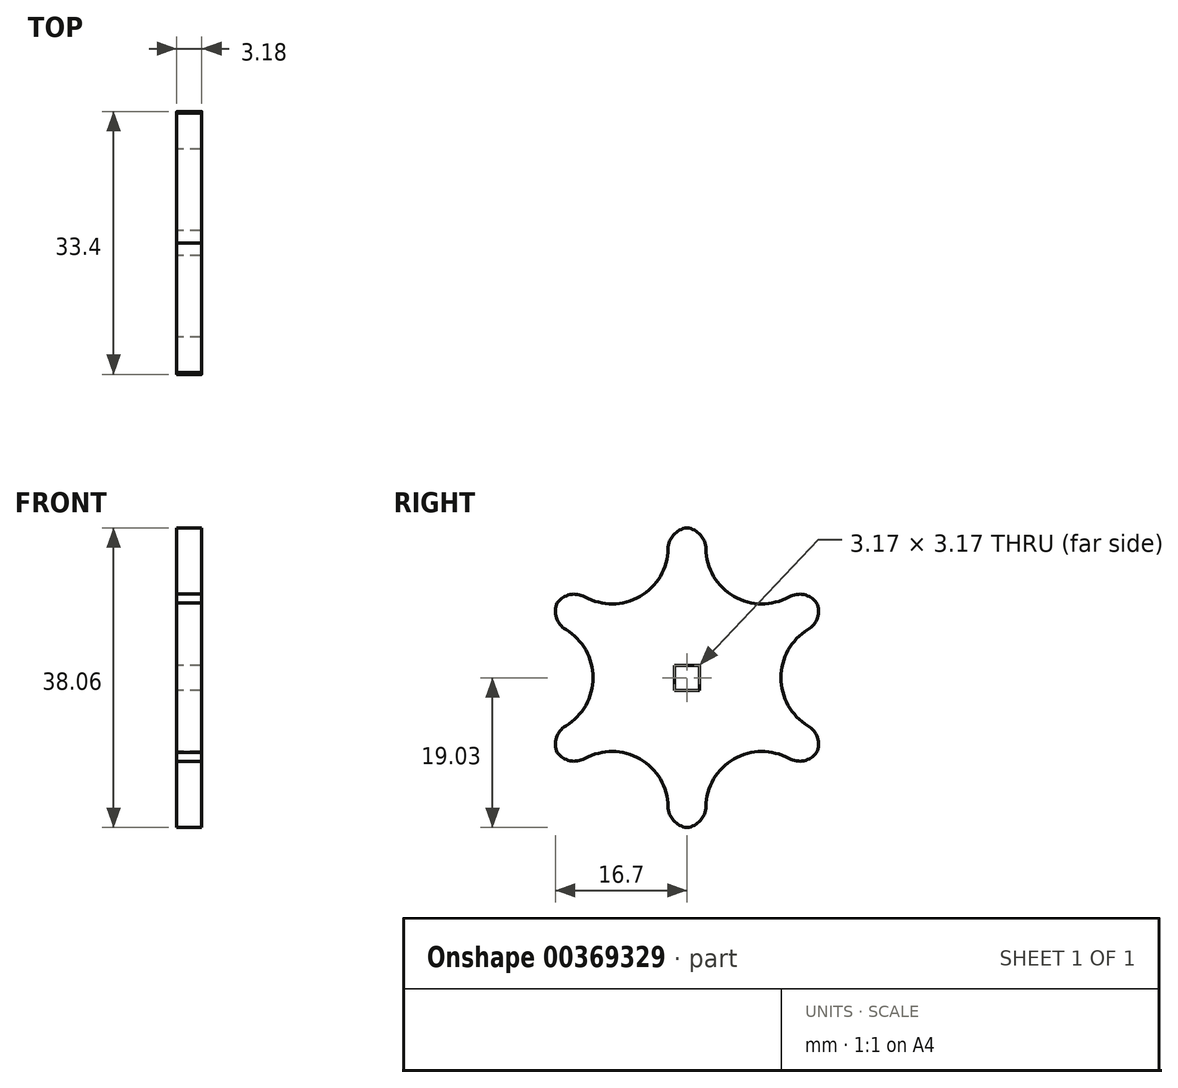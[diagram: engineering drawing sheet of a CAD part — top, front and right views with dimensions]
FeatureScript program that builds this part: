
annotation { "Feature Type Name" : "Feature", "Feature Type Description" : "" }
export const myFeature = defineFeature(function(context is Context, id is Id, definition is map)
    precondition{}
    {
        {
            var Q0;
            Q0=qCreatedBy(makeId("Right.planeOp"),FACE);
            var sketch = newSketch(context, id + "F0", { "sketchPlane" : qUnion([Q0])});
            skCircle(sketch, "E0", {"center": v(0, 0) * mm, "radius": 19.05 * mm});
            skPoint(sketch, "E0.first.point", {"position": v(-5.9, -18.12) * mm});
            skPoint(sketch, "E0.second.point", {"position": v(-11.42, -15.24) * mm});
            skPoint(sketch, "E0.third.point", {"position": v(-11.44, -15.23) * mm});
            skCircle(sketch, "E1", {"center": v(-19.05, 0) * mm, "radius": 7.12 * mm});
            skCircle(sketch, "E2.1.0", {"center": v(-9.53, -16.5) * mm, "radius": 7.12 * mm});
            skCircle(sketch, "E2.2.0", {"center": v(9.52, -16.5) * mm, "radius": 7.12 * mm});
            skCircle(sketch, "E2.3.0", {"center": v(19.05, 0) * mm, "radius": 7.12 * mm});
            skCircle(sketch, "E2.4.0", {"center": v(9.53, 16.5) * mm, "radius": 7.12 * mm});
            skCircle(sketch, "E2.5.0", {"center": v(-9.53, 16.5) * mm, "radius": 7.12 * mm});
            skSolve(sketch);
        }
        {
            var Q0;
            {var subQ1=sQuery(id+"F0.wireOp",EDGE,"E0");var subQ9=sQuery(id+"F0.wireOp",EDGE,"E2.4.0");var subQ10=makeQuery(id+"F0.imprint","INTERSECT",VERTEX,{"disambiguationData":[OD(0.0)],"derivedFrom":[subQ1,subQ9]});Q0=makeQuery(id+"F0.imprint","IMPRINT",FACE,{"disambiguationData":[TD([[makeQuery(id+"F0.imprint","IMPRINT",EDGE,{"disambiguationData":[TD([[subQ10,1.0]])],"derivedFrom":subQ1}),1.0]])]});}
            extrude(context, id + "F1", {"entities" : qUnion([Q0]), "depth" : 3.17 * mm});
        }
        {
            var Q0;
            Q0=makeQuery(id+"F1.opExtrude","CAP_FACE",FACE,{"disambiguationData":[OSD([sQuery(id+"F0.wireOp",EDGE,"E0"),sQuery(id+"F0.wireOp",EDGE,"E1"),sQuery(id+"F0.wireOp",EDGE,"E2.1.0"),sQuery(id+"F0.wireOp",EDGE,"E2.2.0"),sQuery(id+"F0.wireOp",EDGE,"E2.3.0"),sQuery(id+"F0.wireOp",EDGE,"E2.4.0"),sQuery(id+"F0.wireOp",EDGE,"E2.5.0")])],"isStart":true});
            var sketch = newSketch(context, id + "F2", { "sketchPlane" : qUnion([Q0])});
            skLineSegment(sketch, "E3.bottom", {"start": v(1.59, -1.59) * mm, "end": v(-1.59, -1.59) * mm});
            skLineSegment(sketch, "E3.top", {"start": v(1.59, 1.59) * mm, "end": v(-1.59, 1.59) * mm});
            skLineSegment(sketch, "E3.left", {"start": v(1.59, -1.59) * mm, "end": v(1.59, 1.59) * mm});
            skLineSegment(sketch, "E3.right", {"start": v(-1.59, -1.59) * mm, "end": v(-1.59, 1.59) * mm});
            skPoint(sketch, "E3.middle", {"position": v(0, 0) * mm});
            skSolve(sketch);
        }
        {
            var Q0;
            Q0=makeQuery(id+"F2.imprint","IMPRINT",FACE,{"disambiguationData":[TD([[makeQuery(id+"F2.imprint","IMPRINT",EDGE,{"derivedFrom":sQuery(id+"F2.wireOp",EDGE,"E3.bottom")}),-1.0]])]});
            extrude(context, id + "F3", {"entities" : qUnion([Q0]), "operationType" : NewBodyOperationType.REMOVE, "oppositeDirection" : true, "depth" : 25.4 * mm});
        }
        {
            var Q0;
            {var subQ0=sQuery(id+"F0.wireOp",EDGE,"E2.5.0");var subQ1=sQuery(id+"F0.wireOp",EDGE,"E0");Q0=makeQuery(id+"F1.opExtrude","SWEPT_EDGE",EDGE,{"disambiguationData":[OSD([subQ1,subQ0]),TDD([makeQuery(id+"F0.imprint","INTERSECT",VERTEX,{"disambiguationData":[OD(1.0)],"derivedFrom":[subQ1,subQ0]})])]});}
            var Q1;
            {var subQ0=sQuery(id+"F0.wireOp",EDGE,"E1");var subQ1=sQuery(id+"F0.wireOp",EDGE,"E0");Q1=makeQuery(id+"F1.opExtrude","SWEPT_EDGE",EDGE,{"disambiguationData":[OSD([subQ1,subQ0]),TDD([makeQuery(id+"F0.imprint","INTERSECT",VERTEX,{"disambiguationData":[OD(0.0)],"derivedFrom":[subQ1,subQ0]})])]});}
            var Q2;
            {var subQ0=sQuery(id+"F0.wireOp",EDGE,"E1");var subQ1=sQuery(id+"F0.wireOp",EDGE,"E0");Q2=makeQuery(id+"F1.opExtrude","SWEPT_EDGE",EDGE,{"disambiguationData":[OSD([subQ1,subQ0]),TDD([makeQuery(id+"F0.imprint","INTERSECT",VERTEX,{"disambiguationData":[OD(1.0)],"derivedFrom":[subQ1,subQ0]})])]});}
            var Q3;
            {var subQ0=sQuery(id+"F0.wireOp",EDGE,"E2.1.0");var subQ1=sQuery(id+"F0.wireOp",EDGE,"E0");Q3=makeQuery(id+"F1.opExtrude","SWEPT_EDGE",EDGE,{"disambiguationData":[OSD([subQ1,subQ0]),TDD([makeQuery(id+"F0.imprint","INTERSECT",VERTEX,{"disambiguationData":[OD(0.0)],"derivedFrom":[subQ1,subQ0]})])]});}
            var Q4;
            {var subQ0=sQuery(id+"F0.wireOp",EDGE,"E2.1.0");var subQ1=sQuery(id+"F0.wireOp",EDGE,"E0");Q4=makeQuery(id+"F1.opExtrude","SWEPT_EDGE",EDGE,{"disambiguationData":[OSD([subQ1,subQ0]),TDD([makeQuery(id+"F0.imprint","INTERSECT",VERTEX,{"disambiguationData":[OD(1.0)],"derivedFrom":[subQ1,subQ0]})])]});}
            var Q5;
            {var subQ0=sQuery(id+"F0.wireOp",EDGE,"E2.5.0");var subQ1=sQuery(id+"F0.wireOp",EDGE,"E0");Q5=makeQuery(id+"F1.opExtrude","SWEPT_EDGE",EDGE,{"disambiguationData":[OSD([subQ1,subQ0]),TDD([makeQuery(id+"F0.imprint","INTERSECT",VERTEX,{"disambiguationData":[OD(0.0)],"derivedFrom":[subQ1,subQ0]})])]});}
            var Q6;
            {var subQ0=sQuery(id+"F0.wireOp",EDGE,"E2.4.0");var subQ1=sQuery(id+"F0.wireOp",EDGE,"E0");Q6=makeQuery(id+"F1.opExtrude","SWEPT_EDGE",EDGE,{"disambiguationData":[OSD([subQ1,subQ0]),TDD([makeQuery(id+"F0.imprint","INTERSECT",VERTEX,{"disambiguationData":[OD(0.0)],"derivedFrom":[subQ1,subQ0]})])]});}
            var Q7;
            {var subQ0=sQuery(id+"F0.wireOp",EDGE,"E2.4.0");var subQ1=sQuery(id+"F0.wireOp",EDGE,"E0");Q7=makeQuery(id+"F1.opExtrude","SWEPT_EDGE",EDGE,{"disambiguationData":[OSD([subQ1,subQ0]),TDD([makeQuery(id+"F0.imprint","INTERSECT",VERTEX,{"disambiguationData":[OD(1.0)],"derivedFrom":[subQ1,subQ0]})])]});}
            var Q8;
            {var subQ0=sQuery(id+"F0.wireOp",EDGE,"E2.3.0");var subQ1=sQuery(id+"F0.wireOp",EDGE,"E0");Q8=makeQuery(id+"F1.opExtrude","SWEPT_EDGE",EDGE,{"disambiguationData":[OSD([subQ1,subQ0]),TDD([makeQuery(id+"F0.imprint","INTERSECT",VERTEX,{"disambiguationData":[OD(0.0)],"derivedFrom":[subQ1,subQ0]})])]});}
            var Q9;
            {var subQ0=sQuery(id+"F0.wireOp",EDGE,"E2.3.0");var subQ1=sQuery(id+"F0.wireOp",EDGE,"E0");Q9=makeQuery(id+"F1.opExtrude","SWEPT_EDGE",EDGE,{"disambiguationData":[OSD([subQ1,subQ0]),TDD([makeQuery(id+"F0.imprint","INTERSECT",VERTEX,{"disambiguationData":[OD(1.0)],"derivedFrom":[subQ1,subQ0]})])]});}
            var Q10;
            {var subQ0=sQuery(id+"F0.wireOp",EDGE,"E2.2.0");var subQ1=sQuery(id+"F0.wireOp",EDGE,"E0");Q10=makeQuery(id+"F1.opExtrude","SWEPT_EDGE",EDGE,{"disambiguationData":[OSD([subQ1,subQ0]),TDD([makeQuery(id+"F0.imprint","INTERSECT",VERTEX,{"disambiguationData":[OD(1.0)],"derivedFrom":[subQ1,subQ0]})])]});}
            var Q11;
            {var subQ0=sQuery(id+"F0.wireOp",EDGE,"E2.2.0");var subQ1=sQuery(id+"F0.wireOp",EDGE,"E0");Q11=makeQuery(id+"F1.opExtrude","SWEPT_EDGE",EDGE,{"disambiguationData":[OSD([subQ1,subQ0]),TDD([makeQuery(id+"F0.imprint","INTERSECT",VERTEX,{"disambiguationData":[OD(0.0)],"derivedFrom":[subQ1,subQ0]})])]});}
            fillet(context, id + "F4", {"entities" : qUnion([Q0, Q1, Q2, Q3, Q4, Q5, Q6, Q7, Q8, Q9, Q10, Q11]), "radius" : 2.73 * mm, "tangentPropagation" : true, "allowEdgeOverflow" : false});
        }
    });
